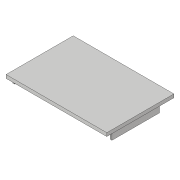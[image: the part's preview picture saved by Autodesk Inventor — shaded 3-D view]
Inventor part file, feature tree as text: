
AUTODESK INVENTOR PART (.ipt)
format: ipt  version: 2018.3 (Build 223284000, 284)  size: 112,640 bytes
history: native  units: in
note: dims shown in document units (in); Inventor stores cm internally (conversion verified against a paired STEP export)
features: extrude x3, sketch x3, projected_geometry x1
ambient origin geometry x8: Origin, YZ Plane, XZ Plane, XY Plane, X Axis, Y Axis, Z Axis, Center Point
bodies: Solid1 (feature_tree)
feature tree (7):
  extrude  "Extrusion1"  Depth=1.258in
  extrude  "Extrusion2"  Depth=0.89in
  extrude  "Extrusion3"  Depth=0.1125in
  sketch  "Sketch1"  dims[d0=1.887in d1=1.258in]
  sketch  "Sketch2"  dims[d2=0.0625in d3=0.0in d4=0.89in]
  projected_geometry  "Projected Loop1"
  sketch  "Sketch3"  dims[d5=0.89in d6=0.1125in d7=0.1125in d8=0.0151in d9=0.0151in d10=0.0323in d11=0.0323in d12=0.1245in d13=0.0in d14=0.0355in d16=0.027in d17=1.856in d18=0.0155in d19=0.0312in d20=0.0in]
